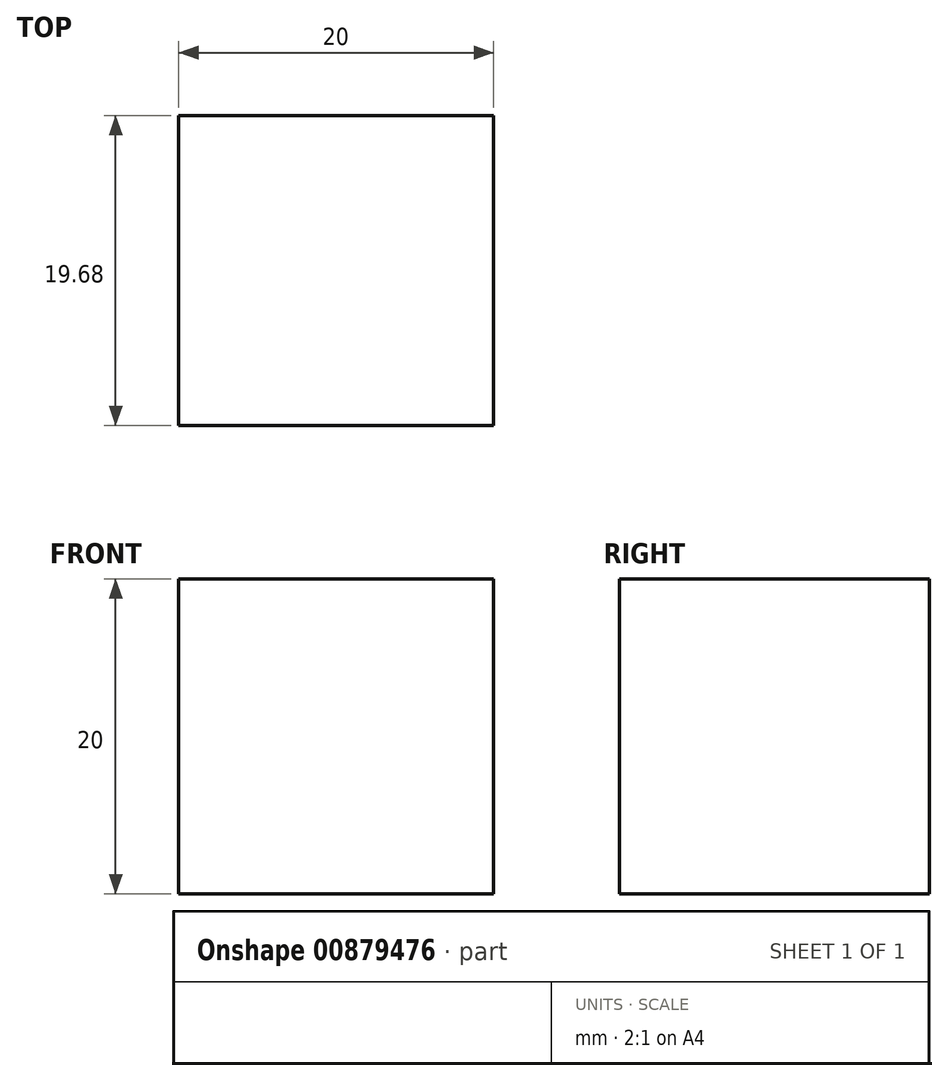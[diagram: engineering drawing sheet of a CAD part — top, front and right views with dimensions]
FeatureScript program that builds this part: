
annotation { "Feature Type Name" : "Feature", "Feature Type Description" : "" }
export const myFeature = defineFeature(function(context is Context, id is Id, definition is map)
    precondition{}
    {
        {
            var Q0;
            Q0=qCreatedBy(makeId("Top.planeOp"),FACE);
            var sketch = newSketch(context, id + "F0", { "sketchPlane" : qUnion([Q0])});
            skLineSegment(sketch, "E0.bottom", {"start": v(10, -9.84) * mm, "end": v(-10, -9.84) * mm});
            skLineSegment(sketch, "E0.top", {"start": v(10, 9.84) * mm, "end": v(-10, 9.84) * mm});
            skLineSegment(sketch, "E0.left", {"start": v(10, -9.84) * mm, "end": v(10, 9.84) * mm});
            skLineSegment(sketch, "E0.right", {"start": v(-10, -9.84) * mm, "end": v(-10, 9.84) * mm});
            skPoint(sketch, "E0.middle", {"position": v(0, 0) * mm});
            skSolve(sketch);
        }
        {
            var Q0;
            Q0=makeQuery(id+"F0.imprint","IMPRINT",FACE,{"disambiguationData":[TD([[makeQuery(id+"F0.imprint","IMPRINT",EDGE,{"derivedFrom":sQuery(id+"F0.wireOp",EDGE,"E0.bottom")}),-1.0]])]});
            extrude(context, id + "F1", {"entities" : qUnion([Q0]), "endBound" : BoundingType.SYMMETRIC, "depth" : 20 * mm, "offsetDistance" : 25 * mm});
        }
    });
